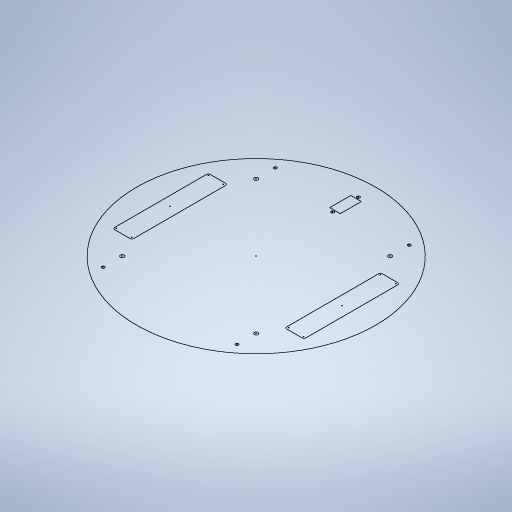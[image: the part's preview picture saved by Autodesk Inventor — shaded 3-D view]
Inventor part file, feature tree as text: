
AUTODESK INVENTOR PART (.ipt)
format: ipt  version: 2023.3 (Build 273359000, 359)  size: 245,760 bytes
history: native  units: mm
features: sketch x1
ambient origin geometry x8: Origin, YZ Plane, XZ Plane, XY Plane, X Axis, Y Axis, Z Axis, Center Point
feature tree (1):
  sketch  "Sketch1"
